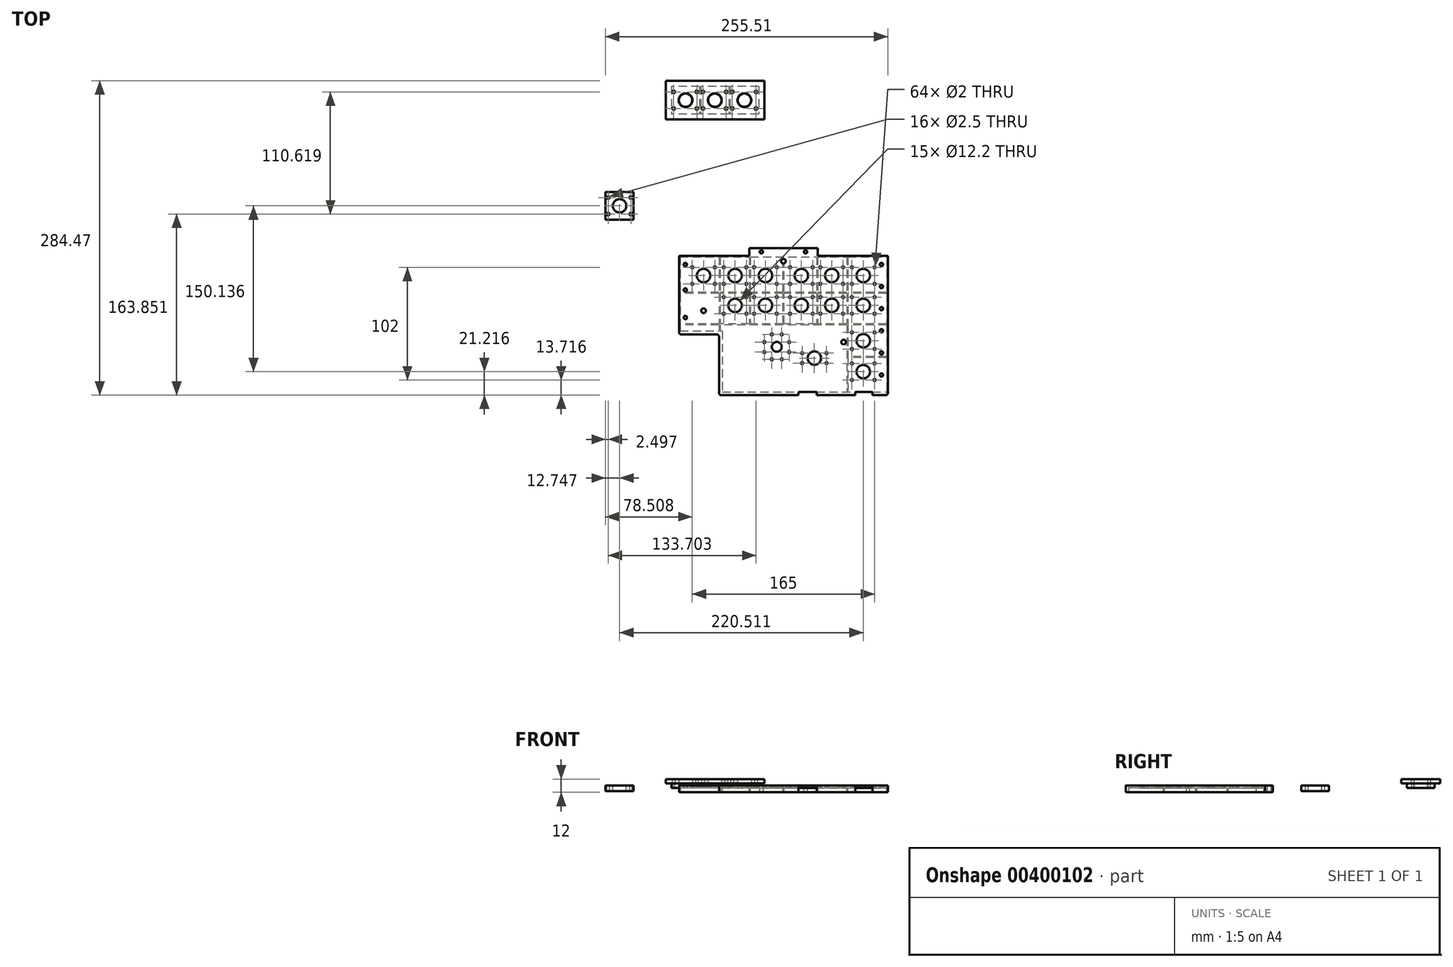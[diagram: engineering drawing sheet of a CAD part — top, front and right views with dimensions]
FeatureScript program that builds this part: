
annotation { "Feature Type Name" : "Feature", "Feature Type Description" : "" }
export const myFeature = defineFeature(function(context is Context, id is Id, definition is map)
    precondition{}
    {
        {
            var Q0;
            Q0=qCreatedBy(makeId("Top.planeOp"),FACE);
            var sketch = newSketch(context, id + "F0", { "sketchPlane" : qUnion([Q0])});
            skLineSegment(sketch, "E0.bottom", {"start": v(7.75, 12.5) * mm, "end": v(-7.75, 12.5) * mm});
            skLineSegment(sketch, "E0.top", {"start": v(7.75, -12.5) * mm, "end": v(-7.75, -12.5) * mm});
            skLineSegment(sketch, "E0.left", {"start": v(7.75, 12.5) * mm, "end": v(7.75, -12.5) * mm});
            skLineSegment(sketch, "E0.right", {"start": v(-7.75, 12.5) * mm, "end": v(-7.75, -12.5) * mm});
            skPoint(sketch, "E0.middle", {"position": v(0, 0) * mm});
            skLineSegment(sketch, "E1.bottom", {"start": v(-7.75, 12.5) * mm, "end": v(-12.75, 12.5) * mm});
            skLineSegment(sketch, "E1.top", {"start": v(-7.75, -12.5) * mm, "end": v(-12.75, -12.5) * mm});
            skLineSegment(sketch, "E1.right", {"start": v(-12.75, 12.5) * mm, "end": v(-12.75, -12.5) * mm});
            skLineSegment(sketch, "E2.bottom", {"start": v(7.75, 12.5) * mm, "end": v(12.75, 12.5) * mm});
            skLineSegment(sketch, "E2.top", {"start": v(7.75, -12.5) * mm, "end": v(12.75, -12.5) * mm});
            skLineSegment(sketch, "E2.right", {"start": v(12.75, 12.5) * mm, "end": v(12.75, -12.5) * mm});
            skCircle(sketch, "E3", {"center": v(-10.75, 7.5) * mm, "radius": 0.9 * mm});
            skPoint(sketch, "E3.centerSnap0", {"position": v(-10.25, 12.5) * mm});
            skCircle(sketch, "E4", {"center": v(-10.75, -7.5) * mm, "radius": 0.9 * mm});
            skCircle(sketch, "E5", {"center": v(10.25, 7.5) * mm, "radius": 0.9 * mm});
            skPoint(sketch, "E5.centerSnap0", {"position": v(10.25, 12.5) * mm});
            skCircle(sketch, "E6", {"center": v(10.25, -7.5) * mm, "radius": 0.9 * mm});
            skCircle(sketch, "E7", {"center": v(0, 0) * mm, "radius": 6 * mm});
            skLineSegment(sketch, "E8.bottom", {"start": v(34.25, 12.5) * mm, "end": v(18.75, 12.5) * mm});
            skLineSegment(sketch, "E8.top", {"start": v(34.25, -12.5) * mm, "end": v(18.75, -12.5) * mm});
            skLineSegment(sketch, "E8.left", {"start": v(34.25, 12.5) * mm, "end": v(34.25, -12.5) * mm});
            skLineSegment(sketch, "E8.right", {"start": v(18.75, 12.5) * mm, "end": v(18.75, -12.5) * mm});
            skPoint(sketch, "E8.middle", {"position": v(26.5, 0) * mm});
            skLineSegment(sketch, "E9.bottom", {"start": v(18.75, 12.5) * mm, "end": v(13.75, 12.5) * mm});
            skLineSegment(sketch, "E9.top", {"start": v(18.75, -12.5) * mm, "end": v(13.75, -12.5) * mm});
            skLineSegment(sketch, "E9.right", {"start": v(13.75, 12.5) * mm, "end": v(13.75, -12.5) * mm});
            skLineSegment(sketch, "E10.bottom", {"start": v(34.25, 12.5) * mm, "end": v(39.25, 12.5) * mm});
            skLineSegment(sketch, "E10.top", {"start": v(34.25, -12.5) * mm, "end": v(39.25, -12.5) * mm});
            skLineSegment(sketch, "E10.right", {"start": v(39.25, 12.5) * mm, "end": v(39.25, -12.5) * mm});
            skCircle(sketch, "E11", {"center": v(15.75, 7.5) * mm, "radius": 0.9 * mm});
            skPoint(sketch, "E11.centerSnap0", {"position": v(16.25, 12.5) * mm});
            skCircle(sketch, "E12", {"center": v(15.75, -7.5) * mm, "radius": 0.9 * mm});
            skCircle(sketch, "E13", {"center": v(36.75, 7.5) * mm, "radius": 0.9 * mm});
            skPoint(sketch, "E13.centerSnap0", {"position": v(36.75, 12.5) * mm});
            skCircle(sketch, "E14", {"center": v(36.75, -7.5) * mm, "radius": 0.9 * mm});
            skCircle(sketch, "E15", {"center": v(26.5, 0) * mm, "radius": 6 * mm});
            skLineSegment(sketch, "E16.bottom", {"start": v(61.25, 12.5) * mm, "end": v(45.25, 12.5) * mm});
            skLineSegment(sketch, "E16.top", {"start": v(61.25, -12.5) * mm, "end": v(45.25, -12.5) * mm});
            skLineSegment(sketch, "E16.left", {"start": v(61.25, 12.5) * mm, "end": v(61.25, -12.5) * mm});
            skLineSegment(sketch, "E16.right", {"start": v(45.25, 12.5) * mm, "end": v(45.25, -12.5) * mm});
            skPoint(sketch, "E16.middle", {"position": v(53.25, 0) * mm});
            skLineSegment(sketch, "E17.bottom", {"start": v(45.25, 12.5) * mm, "end": v(40.25, 12.5) * mm});
            skLineSegment(sketch, "E17.top", {"start": v(45.25, -12.5) * mm, "end": v(40.25, -12.5) * mm});
            skLineSegment(sketch, "E17.right", {"start": v(40.25, 12.5) * mm, "end": v(40.25, -12.5) * mm});
            skLineSegment(sketch, "E18.bottom", {"start": v(61.25, 12.5) * mm, "end": v(66.25, 12.5) * mm});
            skLineSegment(sketch, "E18.top", {"start": v(61.25, -12.5) * mm, "end": v(66.25, -12.5) * mm});
            skLineSegment(sketch, "E18.right", {"start": v(66.25, 12.5) * mm, "end": v(66.25, -12.5) * mm});
            skCircle(sketch, "E19", {"center": v(42.25, 7.5) * mm, "radius": 0.9 * mm});
            skPoint(sketch, "E19.centerSnap0", {"position": v(42.75, 12.5) * mm});
            skCircle(sketch, "E20", {"center": v(42.25, -7.5) * mm, "radius": 0.9 * mm});
            skCircle(sketch, "E21", {"center": v(63.75, 7.5) * mm, "radius": 0.9 * mm});
            skPoint(sketch, "E21.centerSnap0", {"position": v(63.75, 12.5) * mm});
            skCircle(sketch, "E22", {"center": v(63.75, -7.5) * mm, "radius": 0.9 * mm});
            skCircle(sketch, "E23", {"center": v(53.25, 0) * mm, "radius": 6 * mm});
            skSolve(sketch);
        }
        {
            var Q0;
            Q0=makeQuery(id+"F0.imprint","IMPRINT",FACE,{"disambiguationData":[TD([[makeQuery(id+"F0.imprint","IMPRINT",EDGE,{"derivedFrom":sQuery(id+"F0.wireOp",EDGE,"E0.bottom")}),1.0]])]});
            var Q1;
            Q1=makeQuery(id+"F0.imprint","IMPRINT",FACE,{"disambiguationData":[TD([[makeQuery(id+"F0.imprint","IMPRINT",EDGE,{"derivedFrom":sQuery(id+"F0.wireOp",EDGE,"E1.bottom")}),1.0]])]});
            var Q2;
            Q2=makeQuery(id+"F0.imprint","IMPRINT",FACE,{"disambiguationData":[TD([[makeQuery(id+"F0.imprint","IMPRINT",EDGE,{"derivedFrom":sQuery(id+"F0.wireOp",EDGE,"E2.bottom")}),-1.0]])]});
            var Q3;
            Q3=makeQuery(id+"F0.imprint","IMPRINT",FACE,{"disambiguationData":[TD([[makeQuery(id+"F0.imprint","IMPRINT",EDGE,{"derivedFrom":sQuery(id+"F0.wireOp",EDGE,"E9.bottom")}),1.0]])]});
            var Q4;
            Q4=makeQuery(id+"F0.imprint","IMPRINT",FACE,{"disambiguationData":[TD([[makeQuery(id+"F0.imprint","IMPRINT",EDGE,{"derivedFrom":sQuery(id+"F0.wireOp",EDGE,"E8.bottom")}),1.0]])]});
            var Q5;
            Q5=makeQuery(id+"F0.imprint","IMPRINT",FACE,{"disambiguationData":[TD([[makeQuery(id+"F0.imprint","IMPRINT",EDGE,{"derivedFrom":sQuery(id+"F0.wireOp",EDGE,"E10.bottom")}),-1.0]])]});
            var Q6;
            Q6=makeQuery(id+"F0.imprint","IMPRINT",FACE,{"disambiguationData":[TD([[makeQuery(id+"F0.imprint","IMPRINT",EDGE,{"derivedFrom":sQuery(id+"F0.wireOp",EDGE,"E17.bottom")}),1.0]])]});
            var Q7;
            Q7=makeQuery(id+"F0.imprint","IMPRINT",FACE,{"disambiguationData":[TD([[makeQuery(id+"F0.imprint","IMPRINT",EDGE,{"derivedFrom":sQuery(id+"F0.wireOp",EDGE,"E16.bottom")}),1.0]])]});
            var Q8;
            Q8=makeQuery(id+"F0.imprint","IMPRINT",FACE,{"disambiguationData":[TD([[makeQuery(id+"F0.imprint","IMPRINT",EDGE,{"derivedFrom":sQuery(id+"F0.wireOp",EDGE,"E18.bottom")}),-1.0]])]});
            extrude(context, id + "F1", {"entities" : qUnion([Q0, Q1, Q2, Q3, Q4, Q5, Q6, Q7, Q8]), "depth" : 4 * mm});
        }
        {
            var Q0;
            Q0=makeQuery(id+"F1.opExtrude","CAP_FACE",FACE,{"disambiguationData":[OSD([sQuery(id+"F0.wireOp",EDGE,"E0.bottom"),sQuery(id+"F0.wireOp",EDGE,"E0.top"),sQuery(id+"F0.wireOp",EDGE,"E1.bottom"),sQuery(id+"F0.wireOp",EDGE,"E1.top"),sQuery(id+"F0.wireOp",EDGE,"E1.right"),sQuery(id+"F0.wireOp",EDGE,"E2.bottom"),sQuery(id+"F0.wireOp",EDGE,"E2.top"),sQuery(id+"F0.wireOp",EDGE,"E2.right"),sQuery(id+"F0.wireOp",EDGE,"E3"),sQuery(id+"F0.wireOp",EDGE,"E4"),sQuery(id+"F0.wireOp",EDGE,"E5"),sQuery(id+"F0.wireOp",EDGE,"E6"),sQuery(id+"F0.wireOp",EDGE,"E7")])],"isStart":false});
            var sketch = newSketch(context, id + "F2", { "sketchPlane" : qUnion([Q0])});
            skLineSegment(sketch, "E24.bottom", {"start": v(-17.75, 17.5) * mm, "end": v(71.25, 17.5) * mm});
            skLineSegment(sketch, "E24.top", {"start": v(-17.75, -17.5) * mm, "end": v(71.25, -17.5) * mm});
            skLineSegment(sketch, "E24.left", {"start": v(-17.75, 17.5) * mm, "end": v(-17.75, -17.5) * mm});
            skLineSegment(sketch, "E24.right", {"start": v(71.25, 17.5) * mm, "end": v(71.25, -17.5) * mm});
            skCircle(sketch, "E25", {"center": v(-10.75, 7.5) * mm, "radius": 1.25 * mm});
            skCircle(sketch, "E26", {"center": v(-10.75, -7.5) * mm, "radius": 1.25 * mm});
            skCircle(sketch, "E27", {"center": v(10.25, -7.5) * mm, "radius": 1.25 * mm});
            skCircle(sketch, "E28", {"center": v(10.25, 7.5) * mm, "radius": 1.25 * mm});
            skCircle(sketch, "E29", {"center": v(15.75, 7.5) * mm, "radius": 1.25 * mm});
            skCircle(sketch, "E30", {"center": v(15.75, -7.5) * mm, "radius": 1.25 * mm});
            skCircle(sketch, "E31", {"center": v(36.75, -7.5) * mm, "radius": 1.25 * mm});
            skCircle(sketch, "E32", {"center": v(0, 0) * mm, "radius": 6.25 * mm});
            skCircle(sketch, "E33", {"center": v(26.5, 0) * mm, "radius": 6.25 * mm});
            skCircle(sketch, "E34", {"center": v(53.25, 0) * mm, "radius": 6.25 * mm});
            skCircle(sketch, "E35", {"center": v(36.75, 7.5) * mm, "radius": 1.25 * mm});
            skCircle(sketch, "E36", {"center": v(42.25, 7.5) * mm, "radius": 1.25 * mm});
            skCircle(sketch, "E37", {"center": v(42.25, -7.5) * mm, "radius": 1.25 * mm});
            skCircle(sketch, "E38", {"center": v(63.75, 7.5) * mm, "radius": 1.25 * mm});
            skCircle(sketch, "E39", {"center": v(63.75, -7.5) * mm, "radius": 1.25 * mm});
            skSolve(sketch);
        }
        {
            var Q0;
            Q0=qSketchRegion(id+"F2",true);
            extrude(context, id + "F3", {"entities" : qUnion([Q0]), "depth" : 4 * mm});
        }
        {
            var Q0;
            Q0=qCreatedBy(makeId("Top.planeOp"),FACE);
            var sketch = newSketch(context, id + "F4", { "sketchPlane" : qUnion([Q0])});
            skLineSegment(sketch, "E40.bottom", {"start": v(3.56, -143.75) * mm, "end": v(29.06, -143.75) * mm, "construction": true});
            skLineSegment(sketch, "E40.top", {"start": v(3.56, -173.75) * mm, "end": v(29.06, -173.75) * mm, "construction": true});
            skLineSegment(sketch, "E40.left", {"start": v(3.56, -143.75) * mm, "end": v(3.56, -173.75) * mm, "construction": true});
            skLineSegment(sketch, "E40.right", {"start": v(29.06, -143.75) * mm, "end": v(29.06, -173.75) * mm, "construction": true});
            skLineSegment(sketch, "E41.bottom", {"start": v(32.06, -143.75) * mm, "end": v(57.56, -143.75) * mm, "construction": true});
            skLineSegment(sketch, "E41.top", {"start": v(32.06, -173.75) * mm, "end": v(57.56, -173.75) * mm, "construction": true});
            skLineSegment(sketch, "E41.left", {"start": v(32.06, -143.75) * mm, "end": v(32.06, -173.75) * mm, "construction": true});
            skLineSegment(sketch, "E41.right", {"start": v(57.56, -143.75) * mm, "end": v(57.56, -173.75) * mm, "construction": true});
            skLineSegment(sketch, "E42.bottom", {"start": v(119.56, -143.75) * mm, "end": v(145.06, -143.75) * mm, "construction": true});
            skLineSegment(sketch, "E42.top", {"start": v(119.56, -173.75) * mm, "end": v(145.06, -173.75) * mm, "construction": true});
            skLineSegment(sketch, "E42.left", {"start": v(119.56, -143.75) * mm, "end": v(119.56, -173.75) * mm, "construction": true});
            skLineSegment(sketch, "E42.right", {"start": v(145.06, -143.75) * mm, "end": v(145.06, -173.75) * mm, "construction": true});
            skLineSegment(sketch, "E43.bottom", {"start": v(148.06, -143.75) * mm, "end": v(173.56, -143.75) * mm, "construction": true});
            skLineSegment(sketch, "E43.top", {"start": v(148.06, -173.75) * mm, "end": v(173.56, -173.75) * mm, "construction": true});
            skLineSegment(sketch, "E43.left", {"start": v(148.06, -143.75) * mm, "end": v(148.06, -173.75) * mm, "construction": true});
            skLineSegment(sketch, "E43.right", {"start": v(173.56, -143.75) * mm, "end": v(173.56, -173.75) * mm, "construction": true});
            skLineSegment(sketch, "E44.top", {"start": v(148.06, -206.75) * mm, "end": v(173.56, -206.75) * mm, "construction": true});
            skLineSegment(sketch, "E45.bottom", {"start": v(148.06, -209.25) * mm, "end": v(173.56, -209.25) * mm, "construction": true});
            skLineSegment(sketch, "E45.top", {"start": v(148.06, -239.25) * mm, "end": v(173.56, -239.25) * mm, "construction": true});
            skLineSegment(sketch, "E45.left", {"start": v(148.06, -209.25) * mm, "end": v(148.06, -239.25) * mm, "construction": true});
            skLineSegment(sketch, "E45.right", {"start": v(173.56, -209.25) * mm, "end": v(173.56, -239.25) * mm, "construction": true});
            skLineSegment(sketch, "E46.bottom", {"start": v(-4.94, -140.75) * mm, "end": v(182.06, -140.75) * mm});
            skLineSegment(sketch, "E46.top", {"start": v(33.28, -263.97) * mm, "end": v(182.06, -263.97) * mm});
            skLineSegment(sketch, "E46.left", {"start": v(-4.94, -140.75) * mm, "end": v(-4.94, -208.97) * mm});
            skLineSegment(sketch, "E46.right", {"start": v(182.06, -140.75) * mm, "end": v(182.06, -263.97) * mm});
            skLineSegment(sketch, "E47", {"start": v(-4.94, -208.97) * mm, "end": v(33.28, -208.97) * mm});
            skLineSegment(sketch, "E48", {"start": v(33.28, -208.97) * mm, "end": v(33.28, -263.97) * mm});
            skLineSegment(sketch, "E49.bottom", {"start": v(-67.45, -83.12) * mm, "end": v(-51.95, -83.12) * mm});
            skLineSegment(sketch, "E49.top", {"start": v(-67.45, -108.12) * mm, "end": v(-51.95, -108.12) * mm});
            skLineSegment(sketch, "E49.left", {"start": v(-67.45, -83.12) * mm, "end": v(-67.45, -108.12) * mm});
            skLineSegment(sketch, "E49.right", {"start": v(-51.95, -83.12) * mm, "end": v(-51.95, -108.12) * mm});
            skLineSegment(sketch, "E50.bottom", {"start": v(-51.95, -83.12) * mm, "end": v(-46.95, -83.12) * mm});
            skLineSegment(sketch, "E50.top", {"start": v(-51.95, -108.12) * mm, "end": v(-46.95, -108.12) * mm});
            skLineSegment(sketch, "E50.right", {"start": v(-46.95, -83.12) * mm, "end": v(-46.95, -108.12) * mm});
            skLineSegment(sketch, "E51.bottom", {"start": v(-67.45, -83.12) * mm, "end": v(-72.45, -83.12) * mm});
            skLineSegment(sketch, "E51.top", {"start": v(-67.45, -108.12) * mm, "end": v(-72.45, -108.12) * mm});
            skLineSegment(sketch, "E51.right", {"start": v(-72.45, -83.12) * mm, "end": v(-72.45, -108.12) * mm});
            skCircle(sketch, "E52", {"center": v(-59.7, -95.62) * mm, "radius": 6.1 * mm});
            skPoint(sketch, "E52.centerSnap0", {"position": v(-67.45, -95.62) * mm});
            skPoint(sketch, "E52.centerSnap1", {"position": v(-59.7, -83.12) * mm});
            skCircle(sketch, "E53", {"center": v(-69.95, -88.12) * mm, "radius": 1.25 * mm});
            skPoint(sketch, "E53.centerSnap0", {"position": v(-69.95, -83.12) * mm});
            skCircle(sketch, "E54", {"center": v(-69.95, -103.12) * mm, "radius": 1.25 * mm});
            skCircle(sketch, "E55", {"center": v(-49.45, -88.12) * mm, "radius": 1.25 * mm});
            skPoint(sketch, "E55.centerSnap0", {"position": v(-49.45, -83.12) * mm});
            skCircle(sketch, "E56", {"center": v(-49.45, -103.12) * mm, "radius": 1.25 * mm});
            skLineSegment(sketch, "E57.bottom", {"start": v(3.56, -146.25) * mm, "end": v(8.56, -146.25) * mm, "construction": true});
            skLineSegment(sketch, "E57.top", {"start": v(3.56, -171.25) * mm, "end": v(8.56, -171.25) * mm, "construction": true});
            skLineSegment(sketch, "E57.left", {"start": v(3.56, -146.25) * mm, "end": v(3.56, -171.25) * mm, "construction": true});
            skLineSegment(sketch, "E57.right", {"start": v(8.56, -146.25) * mm, "end": v(8.56, -171.25) * mm, "construction": true});
            skLineSegment(sketch, "E58.bottom", {"start": v(29.06, -146.25) * mm, "end": v(24.06, -146.25) * mm, "construction": true});
            skLineSegment(sketch, "E58.top", {"start": v(29.06, -171.25) * mm, "end": v(24.06, -171.25) * mm, "construction": true});
            skLineSegment(sketch, "E58.left", {"start": v(29.06, -146.25) * mm, "end": v(29.06, -171.25) * mm, "construction": true});
            skLineSegment(sketch, "E58.right", {"start": v(24.06, -146.25) * mm, "end": v(24.06, -171.25) * mm, "construction": true});
            skCircle(sketch, "E59", {"center": v(6.06, -151.25) * mm, "radius": 1 * mm});
            skPoint(sketch, "E59.centerSnap0", {"position": v(6.06, -146.25) * mm});
            skCircle(sketch, "E60", {"center": v(6.06, -166.25) * mm, "radius": 1 * mm});
            skCircle(sketch, "E61", {"center": v(16.3, -158.75) * mm, "radius": 6.1 * mm});
            skPoint(sketch, "E61.centerSnap0", {"position": v(8.56, -158.75) * mm});
            skPoint(sketch, "E61.centerSnap1", {"position": v(16.3, -143.75) * mm});
            skCircle(sketch, "E62", {"center": v(26.56, -151.25) * mm, "radius": 1 * mm});
            skPoint(sketch, "E62.centerSnap0", {"position": v(26.56, -146.25) * mm});
            skCircle(sketch, "E63", {"center": v(26.56, -166.25) * mm, "radius": 1 * mm});
            skCircle(sketch, "E64", {"center": v(105.56, -228.97) * mm, "radius": 1 * mm});
            skCircle(sketch, "E65", {"center": v(105.56, -237.97) * mm, "radius": 1 * mm});
            skCircle(sketch, "E66", {"center": v(127.56, -228.97) * mm, "radius": 1 * mm});
            skCircle(sketch, "E67", {"center": v(127.56, -237.97) * mm, "radius": 1 * mm});
            skLineSegment(sketch, "E68.bottom", {"start": v(151.56, -240.25) * mm, "end": v(173.56, -240.25) * mm, "construction": true});
            skLineSegment(sketch, "E68.top", {"start": v(151.56, -262.25) * mm, "end": v(173.56, -262.25) * mm, "construction": true});
            skLineSegment(sketch, "E68.left", {"start": v(151.56, -240.25) * mm, "end": v(151.56, -262.25) * mm, "construction": true});
            skLineSegment(sketch, "E68.right", {"start": v(173.56, -240.25) * mm, "end": v(173.56, -262.25) * mm, "construction": true});
            skLineSegment(sketch, "E69.bottom", {"start": v(154.8, -239.75) * mm, "end": v(166.8, -239.75) * mm, "construction": true});
            skLineSegment(sketch, "E69.top", {"start": v(154.8, -251.75) * mm, "end": v(166.8, -251.75) * mm, "construction": true});
            skLineSegment(sketch, "E69.left", {"start": v(154.8, -239.75) * mm, "end": v(154.8, -251.75) * mm, "construction": true});
            skLineSegment(sketch, "E69.right", {"start": v(166.8, -239.75) * mm, "end": v(166.8, -251.75) * mm, "construction": true});
            skLineSegment(sketch, "E70.bottom", {"start": v(32.06, -146.25) * mm, "end": v(37.06, -146.25) * mm, "construction": true});
            skLineSegment(sketch, "E70.top", {"start": v(32.06, -171.25) * mm, "end": v(37.06, -171.25) * mm, "construction": true});
            skLineSegment(sketch, "E70.left", {"start": v(32.06, -146.25) * mm, "end": v(32.06, -171.25) * mm, "construction": true});
            skLineSegment(sketch, "E70.right", {"start": v(37.06, -146.25) * mm, "end": v(37.06, -171.25) * mm, "construction": true});
            skLineSegment(sketch, "E71.bottom", {"start": v(57.56, -146.25) * mm, "end": v(52.56, -146.25) * mm, "construction": true});
            skLineSegment(sketch, "E71.top", {"start": v(57.56, -171.25) * mm, "end": v(52.56, -171.25) * mm, "construction": true});
            skLineSegment(sketch, "E71.left", {"start": v(57.56, -146.25) * mm, "end": v(57.56, -171.25) * mm, "construction": true});
            skLineSegment(sketch, "E71.right", {"start": v(52.56, -146.25) * mm, "end": v(52.56, -171.25) * mm, "construction": true});
            skCircle(sketch, "E72", {"center": v(34.56, -151.25) * mm, "radius": 1 * mm});
            skPoint(sketch, "E72.centerSnap0", {"position": v(34.56, -146.25) * mm});
            skCircle(sketch, "E73", {"center": v(34.56, -166.25) * mm, "radius": 1 * mm});
            skCircle(sketch, "E74", {"center": v(55.06, -151.25) * mm, "radius": 1 * mm});
            skPoint(sketch, "E74.centerSnap0", {"position": v(55.06, -146.25) * mm});
            skCircle(sketch, "E75", {"center": v(55.06, -166.25) * mm, "radius": 1 * mm});
            skCircle(sketch, "E76", {"center": v(44.8, -158.75) * mm, "radius": 6.1 * mm});
            skPoint(sketch, "E76.centerSnap0", {"position": v(37.06, -158.75) * mm});
            skPoint(sketch, "E76.centerSnap1", {"position": v(44.8, -143.75) * mm});
            skLineSegment(sketch, "E77.bottom", {"start": v(119.56, -146.25) * mm, "end": v(124.56, -146.25) * mm, "construction": true});
            skLineSegment(sketch, "E77.top", {"start": v(119.56, -171.25) * mm, "end": v(124.56, -171.25) * mm, "construction": true});
            skLineSegment(sketch, "E77.left", {"start": v(119.56, -146.25) * mm, "end": v(119.56, -171.25) * mm, "construction": true});
            skLineSegment(sketch, "E77.right", {"start": v(124.56, -146.25) * mm, "end": v(124.56, -171.25) * mm, "construction": true});
            skLineSegment(sketch, "E78.bottom", {"start": v(145.06, -146.25) * mm, "end": v(140.06, -146.25) * mm, "construction": true});
            skLineSegment(sketch, "E78.top", {"start": v(145.06, -171.25) * mm, "end": v(140.06, -171.25) * mm, "construction": true});
            skLineSegment(sketch, "E78.left", {"start": v(145.06, -146.25) * mm, "end": v(145.06, -171.25) * mm, "construction": true});
            skLineSegment(sketch, "E78.right", {"start": v(140.06, -146.25) * mm, "end": v(140.06, -171.25) * mm, "construction": true});
            skLineSegment(sketch, "E79.bottom", {"start": v(148.06, -146.25) * mm, "end": v(153.06, -146.25) * mm, "construction": true});
            skLineSegment(sketch, "E79.top", {"start": v(148.06, -171.25) * mm, "end": v(153.06, -171.25) * mm, "construction": true});
            skLineSegment(sketch, "E79.left", {"start": v(148.06, -146.25) * mm, "end": v(148.06, -171.25) * mm, "construction": true});
            skLineSegment(sketch, "E79.right", {"start": v(153.06, -146.25) * mm, "end": v(153.06, -171.25) * mm, "construction": true});
            skLineSegment(sketch, "E80.bottom", {"start": v(173.56, -146.25) * mm, "end": v(168.56, -146.25) * mm, "construction": true});
            skLineSegment(sketch, "E80.top", {"start": v(173.56, -171.25) * mm, "end": v(168.56, -171.25) * mm, "construction": true});
            skLineSegment(sketch, "E80.left", {"start": v(173.56, -146.25) * mm, "end": v(173.56, -171.25) * mm, "construction": true});
            skLineSegment(sketch, "E80.right", {"start": v(168.56, -146.25) * mm, "end": v(168.56, -171.25) * mm, "construction": true});
            skLineSegment(sketch, "E81.top", {"start": v(148.06, -204.25) * mm, "end": v(153.06, -204.25) * mm, "construction": true});
            skLineSegment(sketch, "E82.top", {"start": v(173.56, -204.25) * mm, "end": v(168.56, -204.25) * mm, "construction": true});
            skLineSegment(sketch, "E83.bottom", {"start": v(148.06, -205.25) * mm, "end": v(153.06, -205.25) * mm, "construction": true});
            skLineSegment(sketch, "E83.top", {"start": v(148.06, -230.25) * mm, "end": v(153.06, -230.25) * mm, "construction": true});
            skLineSegment(sketch, "E83.left", {"start": v(148.06, -205.25) * mm, "end": v(148.06, -230.25) * mm, "construction": true});
            skLineSegment(sketch, "E83.right", {"start": v(153.06, -205.25) * mm, "end": v(153.06, -230.25) * mm, "construction": true});
            skLineSegment(sketch, "E84.bottom", {"start": v(173.56, -205.25) * mm, "end": v(168.56, -205.25) * mm, "construction": true});
            skLineSegment(sketch, "E84.top", {"start": v(173.56, -230.25) * mm, "end": v(168.56, -230.25) * mm, "construction": true});
            skLineSegment(sketch, "E84.left", {"start": v(173.56, -205.25) * mm, "end": v(173.56, -230.25) * mm, "construction": true});
            skLineSegment(sketch, "E84.right", {"start": v(168.56, -205.25) * mm, "end": v(168.56, -230.25) * mm, "construction": true});
            skCircle(sketch, "E85", {"center": v(62.06, -178.25) * mm, "radius": 1 * mm});
            skCircle(sketch, "E86", {"center": v(62.06, -193.25) * mm, "radius": 1 * mm});
            skCircle(sketch, "E87", {"center": v(82.56, -178.25) * mm, "radius": 1 * mm});
            skCircle(sketch, "E88", {"center": v(82.56, -193.25) * mm, "radius": 1 * mm});
            skCircle(sketch, "E89", {"center": v(72.3, -185.75) * mm, "radius": 6.1 * mm});
            skCircle(sketch, "E90", {"center": v(82.56, -223.25) * mm, "radius": 4.5 * mm});
            skCircle(sketch, "E91", {"center": v(71.3, -219) * mm, "radius": 1 * mm});
            skCircle(sketch, "E92", {"center": v(71.3, -228) * mm, "radius": 1 * mm});
            skCircle(sketch, "E93", {"center": v(93.8, -219) * mm, "radius": 1 * mm});
            skCircle(sketch, "E94", {"center": v(93.8, -228) * mm, "radius": 1 * mm});
            skCircle(sketch, "E95", {"center": v(94.56, -178.25) * mm, "radius": 1 * mm});
            skCircle(sketch, "E96", {"center": v(94.56, -193.25) * mm, "radius": 1 * mm});
            skCircle(sketch, "E97", {"center": v(115.06, -178.25) * mm, "radius": 1 * mm});
            skCircle(sketch, "E98", {"center": v(115.06, -193.25) * mm, "radius": 1 * mm});
            skCircle(sketch, "E99", {"center": v(122.06, -151.25) * mm, "radius": 1 * mm});
            skPoint(sketch, "E99.centerSnap0", {"position": v(122.06, -146.25) * mm});
            skCircle(sketch, "E100", {"center": v(122.06, -166.25) * mm, "radius": 1 * mm});
            skCircle(sketch, "E101", {"center": v(132.3, -158.75) * mm, "radius": 6.1 * mm});
            skPoint(sketch, "E101.centerSnap0", {"position": v(124.56, -158.75) * mm});
            skPoint(sketch, "E101.centerSnap1", {"position": v(132.3, -143.75) * mm});
            skCircle(sketch, "E102", {"center": v(142.56, -151.25) * mm, "radius": 1 * mm});
            skPoint(sketch, "E102.centerSnap0", {"position": v(142.56, -146.25) * mm});
            skCircle(sketch, "E103", {"center": v(142.56, -166.25) * mm, "radius": 1 * mm});
            skCircle(sketch, "E104", {"center": v(150.56, -151.25) * mm, "radius": 1 * mm});
            skPoint(sketch, "E104.centerSnap0", {"position": v(150.56, -146.25) * mm});
            skCircle(sketch, "E105", {"center": v(150.56, -166.25) * mm, "radius": 1 * mm});
            skCircle(sketch, "E106", {"center": v(171.06, -151.25) * mm, "radius": 1 * mm});
            skPoint(sketch, "E106.centerSnap0", {"position": v(171.06, -146.25) * mm});
            skCircle(sketch, "E107", {"center": v(171.06, -166.25) * mm, "radius": 1 * mm});
            skCircle(sketch, "E108", {"center": v(160.8, -158.75) * mm, "radius": 6.1 * mm});
            skPoint(sketch, "E108.centerSnap0", {"position": v(153.06, -158.75) * mm});
            skPoint(sketch, "E108.centerSnap1", {"position": v(160.8, -143.75) * mm});
            skCircle(sketch, "E109", {"center": v(16.3, -190.57) * mm, "radius": 2.1 * mm});
            skCircle(sketch, "E110", {"center": v(143.06, -218.97) * mm, "radius": 2.1 * mm});
            skCircle(sketch, "E111", {"center": v(150.56, -210.25) * mm, "radius": 1 * mm});
            skPoint(sketch, "E111.centerSnap0", {"position": v(150.56, -205.25) * mm});
            skCircle(sketch, "E112", {"center": v(150.56, -225.25) * mm, "radius": 1 * mm});
            skCircle(sketch, "E113", {"center": v(171.06, -210.25) * mm, "radius": 1 * mm});
            skPoint(sketch, "E113.centerSnap0", {"position": v(171.06, -205.25) * mm});
            skCircle(sketch, "E114", {"center": v(171.06, -225.25) * mm, "radius": 1 * mm});
            skCircle(sketch, "E115", {"center": v(160.8, -217.75) * mm, "radius": 6.1 * mm});
            skPoint(sketch, "E115.centerSnap0", {"position": v(153.06, -217.75) * mm});
            skCircle(sketch, "E116", {"center": v(160.8, -245.75) * mm, "radius": 6.1 * mm});
            skPoint(sketch, "E116.centerSnap0", {"position": v(160.8, -239.75) * mm});
            skPoint(sketch, "E116.centerSnap1", {"position": v(154.8, -245.75) * mm});
            skCircle(sketch, "E117", {"center": v(-0.2, -148.75) * mm, "radius": 1.5 * mm});
            skCircle(sketch, "E118", {"center": v(-0.2, -171.75) * mm, "radius": 1.5 * mm});
            skCircle(sketch, "E119", {"center": v(177.3, -208.75) * mm, "radius": 1.5 * mm});
            skCircle(sketch, "E120", {"center": v(177.3, -228.75) * mm, "radius": 1.5 * mm});
            skCircle(sketch, "E121", {"center": v(177.3, -248.75) * mm, "radius": 1.5 * mm});
            skCircle(sketch, "E122", {"center": v(177.3, -168.75) * mm, "radius": 1.5 * mm});
            skCircle(sketch, "E123", {"center": v(177.3, -188.75) * mm, "radius": 1.5 * mm});
            skCircle(sketch, "E124", {"center": v(177.3, -148.75) * mm, "radius": 1.5 * mm});
            skCircle(sketch, "E125", {"center": v(150.56, -238.25) * mm, "radius": 1 * mm});
            skCircle(sketch, "E126", {"center": v(150.56, -253.25) * mm, "radius": 1 * mm});
            skCircle(sketch, "E127", {"center": v(171.06, -238.25) * mm, "radius": 1 * mm});
            skCircle(sketch, "E128", {"center": v(171.06, -253.25) * mm, "radius": 1 * mm});
            skCircle(sketch, "E129", {"center": v(-0.2, -196.75) * mm, "radius": 1.5 * mm});
            skLineSegment(sketch, "E130.bottom", {"start": v(58.56, -140.75) * mm, "end": v(118.56, -140.75) * mm});
            skLineSegment(sketch, "E130.top", {"start": v(58.56, -133.75) * mm, "end": v(118.56, -133.75) * mm});
            skLineSegment(sketch, "E130.left", {"start": v(58.56, -140.75) * mm, "end": v(58.56, -133.75) * mm});
            skLineSegment(sketch, "E130.right", {"start": v(118.56, -140.75) * mm, "end": v(118.56, -133.75) * mm});
            skCircle(sketch, "E131", {"center": v(68.56, -137.25) * mm, "radius": 1.5 * mm});
            skCircle(sketch, "E132", {"center": v(108.56, -137.25) * mm, "radius": 1.5 * mm});
            skCircle(sketch, "E133", {"center": v(116.56, -233.47) * mm, "radius": 6.1 * mm});
            skCircle(sketch, "E134", {"center": v(82.56, -223.25) * mm, "radius": 12.5 * mm, "construction": true});
            skCircle(sketch, "E135", {"center": v(44.8, -185.75) * mm, "radius": 6.1 * mm});
            skCircle(sketch, "E136", {"center": v(34.56, -178.25) * mm, "radius": 1 * mm});
            skCircle(sketch, "E137", {"center": v(34.56, -193.25) * mm, "radius": 1 * mm});
            skCircle(sketch, "E138", {"center": v(55.06, -178.25) * mm, "radius": 1 * mm});
            skCircle(sketch, "E139", {"center": v(55.06, -193.25) * mm, "radius": 1 * mm});
            skCircle(sketch, "E140", {"center": v(122.06, -193.25) * mm, "radius": 1 * mm});
            skCircle(sketch, "E141", {"center": v(142.56, -193.25) * mm, "radius": 1 * mm});
            skLineSegment(sketch, "E142", {"start": v(223.04, -262.25) * mm, "end": v(194.25, -262.25) * mm, "construction": true});
            skCircle(sketch, "E143", {"center": v(78.06, -212) * mm, "radius": 1 * mm});
            skCircle(sketch, "E144", {"center": v(87.06, -212) * mm, "radius": 1 * mm});
            skCircle(sketch, "E145", {"center": v(78.06, -234.5) * mm, "radius": 1 * mm});
            skCircle(sketch, "E146", {"center": v(87.06, -234.5) * mm, "radius": 1 * mm});
            skCircle(sketch, "E147", {"center": v(104.8, -185.75) * mm, "radius": 6.1 * mm});
            skCircle(sketch, "E148", {"center": v(132.3, -185.75) * mm, "radius": 6.1 * mm});
            skCircle(sketch, "E149", {"center": v(122.06, -178.25) * mm, "radius": 1 * mm});
            skCircle(sketch, "E150", {"center": v(142.56, -178.25) * mm, "radius": 1 * mm});
            skCircle(sketch, "E151", {"center": v(160.8, -185.75) * mm, "radius": 6.1 * mm});
            skCircle(sketch, "E152", {"center": v(150.56, -178.25) * mm, "radius": 1 * mm});
            skCircle(sketch, "E153", {"center": v(150.56, -193.25) * mm, "radius": 1 * mm});
            skCircle(sketch, "E154", {"center": v(171.06, -178.25) * mm, "radius": 1 * mm});
            skPoint(sketch, "E154.centerSnap0", {"position": v(171.06, -171.25) * mm});
            skCircle(sketch, "E155", {"center": v(171.06, -193.25) * mm, "radius": 1 * mm});
            skCircle(sketch, "E156", {"center": v(104.8, -158.75) * mm, "radius": 6.1 * mm});
            skCircle(sketch, "E157", {"center": v(115.06, -151.25) * mm, "radius": 1 * mm});
            skCircle(sketch, "E158", {"center": v(115.06, -166.25) * mm, "radius": 1 * mm});
            skCircle(sketch, "E159", {"center": v(94.56, -151.25) * mm, "radius": 1 * mm});
            skCircle(sketch, "E160", {"center": v(94.56, -166.25) * mm, "radius": 1 * mm});
            skCircle(sketch, "E161", {"center": v(72.3, -158.75) * mm, "radius": 6.1 * mm});
            skCircle(sketch, "E162", {"center": v(82.56, -151.25) * mm, "radius": 1 * mm});
            skCircle(sketch, "E163", {"center": v(82.56, -166.25) * mm, "radius": 1 * mm});
            skCircle(sketch, "E164", {"center": v(62.06, -151.25) * mm, "radius": 1 * mm});
            skCircle(sketch, "E165", {"center": v(62.06, -166.25) * mm, "radius": 1 * mm});
            skCircle(sketch, "E166", {"center": v(88.56, -145.75) * mm, "radius": 2.1 * mm});
            skSolve(sketch);
        }
        {
            var Q0;
            Q0=makeQuery(id+"F4.imprint","IMPRINT",FACE,{"disambiguationData":[TD([[makeQuery(id+"F4.imprint","IMPRINT",EDGE,{"derivedFrom":sQuery(id+"F4.wireOp",EDGE,"E49.bottom")}),-1.0]])]});
            var Q1;
            Q1=makeQuery(id+"F4.imprint","IMPRINT",FACE,{"disambiguationData":[TD([[makeQuery(id+"F4.imprint","IMPRINT",EDGE,{"derivedFrom":sQuery(id+"F4.wireOp",EDGE,"E51.bottom")}),1.0]])]});
            var Q2;
            Q2=makeQuery(id+"F4.imprint","IMPRINT",FACE,{"disambiguationData":[TD([[makeQuery(id+"F4.imprint","IMPRINT",EDGE,{"derivedFrom":sQuery(id+"F4.wireOp",EDGE,"E50.bottom")}),-1.0]])]});
            extrude(context, id + "F5", {"entities" : qUnion([Q0, Q1, Q2]), "oppositeDirection" : true, "depth" : 3 * mm});
        }
        {
            var Q0;
            Q0=qSketchRegion(id+"F4",true);
            extrude(context, id + "F6", {"entities" : qUnion([Q0]), "operationType" : NewBodyOperationType.ADD, "depth" : 2 * mm});
        }
        {
            var Q0;
            Q0=makeQuery(id+"F4.imprint","IMPRINT",FACE,{"disambiguationData":[TD([[makeQuery(id+"F4.imprint","IMPRINT",EDGE,{"derivedFrom":sQuery(id+"F4.wireOp",EDGE,"E46.bottom")}),-1.0]])]});
            var sketch = newSketch(context, id + "F7", { "sketchPlane" : qUnion([Q0])});
            skLineSegment(sketch, "E167", {"start": v(191, -174) * mm, "end": v(196.06, -174) * mm, "construction": true});
            skLineSegment(sketch, "E168", {"start": v(187.13, -202.5) * mm, "end": v(195.16, -202.5) * mm, "construction": true});
            skLineSegment(sketch, "E169", {"start": v(185.67, -231.87) * mm, "end": v(191.23, -231.87) * mm, "construction": true});
            skLineSegment(sketch, "E170", {"start": v(147.06, -137.55) * mm, "end": v(147.06, -134.13) * mm, "construction": true});
            skLineSegment(sketch, "E171", {"start": v(119.6, -132.5) * mm, "end": v(119.6, -129.45) * mm, "construction": true});
            skLineSegment(sketch, "E172", {"start": v(58.56, -132.83) * mm, "end": v(58.56, -129.85) * mm, "construction": true});
            skLineSegment(sketch, "E173", {"start": v(31.28, -136.19) * mm, "end": v(31.28, -132.5) * mm, "construction": true});
            skLineSegment(sketch, "E174.bottom", {"start": v(182.06, -174) * mm, "end": v(147.06, -174) * mm});
            skLineSegment(sketch, "E174.top", {"start": v(182.06, -175) * mm, "end": v(147.06, -175) * mm});
            skLineSegment(sketch, "E174.left", {"start": v(182.06, -174) * mm, "end": v(182.06, -175) * mm});
            skLineSegment(sketch, "E174.right", {"start": v(-4.94, -174) * mm, "end": v(-4.94, -175) * mm});
            skLineSegment(sketch, "E175.bottom", {"start": v(182.06, -202.5) * mm, "end": v(147.06, -202.5) * mm});
            skLineSegment(sketch, "E175.top", {"start": v(182.06, -203.5) * mm, "end": v(147.06, -203.5) * mm});
            skLineSegment(sketch, "E175.left", {"start": v(182.06, -202.5) * mm, "end": v(182.06, -203.5) * mm});
            skLineSegment(sketch, "E175.right", {"start": v(-4.94, -202.5) * mm, "end": v(-4.94, -203.5) * mm});
            skLineSegment(sketch, "E176", {"start": v(194.32, -140.75) * mm, "end": v(196.06, -263.96) * mm, "construction": true});
            skLineSegment(sketch, "E177", {"start": v(190.9, -263.96) * mm, "end": v(185.03, -263.96) * mm, "construction": true});
            skLineSegment(sketch, "E178.bottom", {"start": v(182.06, -231.87) * mm, "end": v(147.06, -231.87) * mm});
            skLineSegment(sketch, "E178.top", {"start": v(182.06, -232.87) * mm, "end": v(147.06, -232.87) * mm});
            skLineSegment(sketch, "E178.left", {"start": v(182.06, -231.87) * mm, "end": v(182.06, -232.87) * mm});
            skLineSegment(sketch, "E179", {"start": v(-4.94, -139.37) * mm, "end": v(-4.94, -137.02) * mm, "construction": true});
            skLineSegment(sketch, "E180", {"start": v(-7.3, -140.75) * mm, "end": v(-12.92, -140.75) * mm, "construction": true});
            skLineSegment(sketch, "E181.bottom", {"start": v(-4.94, -140.75) * mm, "end": v(146.06, -140.75) * mm});
            skLineSegment(sketch, "E181.top", {"start": v(-4.94, -141.75) * mm, "end": v(146.06, -141.75) * mm});
            skLineSegment(sketch, "E181.left", {"start": v(-4.94, -140.75) * mm, "end": v(-4.94, -141.75) * mm});
            skLineSegment(sketch, "E181.right", {"start": v(182.06, -140.75) * mm, "end": v(182.06, -141.75) * mm});
            skLineSegment(sketch, "E182.bottom", {"start": v(147.06, -140.75) * mm, "end": v(146.06, -140.75) * mm});
            skLineSegment(sketch, "E182.top", {"start": v(147.06, -263.96) * mm, "end": v(146.06, -263.96) * mm});
            skLineSegment(sketch, "E182.left", {"start": v(147.06, -141.75) * mm, "end": v(147.06, -174) * mm});
            skLineSegment(sketch, "E182.right", {"start": v(146.06, -141.75) * mm, "end": v(146.06, -174) * mm});
            skLineSegment(sketch, "E183.trimOffspring", {"start": v(147.06, -175) * mm, "end": v(147.06, -202.5) * mm});
            skLineSegment(sketch, "E184.trimOffspring", {"start": v(146.06, -174) * mm, "end": v(119.6, -174) * mm});
            skLineSegment(sketch, "E185.trimOffspring", {"start": v(146.06, -175) * mm, "end": v(146.06, -202.5) * mm});
            skLineSegment(sketch, "E186.trimOffspring", {"start": v(146.06, -175) * mm, "end": v(119.6, -175) * mm});
            skLineSegment(sketch, "E187.trimOffspring", {"start": v(146.06, -202.5) * mm, "end": v(119.6, -202.5) * mm});
            skLineSegment(sketch, "E188.trimOffspring", {"start": v(147.06, -203.5) * mm, "end": v(147.06, -231.87) * mm});
            skLineSegment(sketch, "E189.trimOffspring", {"start": v(146.06, -203.5) * mm, "end": v(58.56, -203.5) * mm});
            skLineSegment(sketch, "E190.trimOffspring", {"start": v(146.06, -203.5) * mm, "end": v(146.06, -263.96) * mm});
            skLineSegment(sketch, "E191.trimOffspring", {"start": v(147.06, -232.87) * mm, "end": v(147.06, -263.96) * mm});
            skLineSegment(sketch, "E192.trimOffspring", {"start": v(147.06, -140.75) * mm, "end": v(182.06, -140.75) * mm});
            skLineSegment(sketch, "E193.trimOffspring", {"start": v(147.06, -141.75) * mm, "end": v(182.06, -141.75) * mm});
            skLineSegment(sketch, "E194.bottom", {"start": v(119.6, -140.75) * mm, "end": v(118.6, -140.75) * mm});
            skLineSegment(sketch, "E194.left", {"start": v(119.6, -140.75) * mm, "end": v(119.6, -174) * mm});
            skLineSegment(sketch, "E194.right", {"start": v(118.6, -140.75) * mm, "end": v(118.6, -174) * mm});
            skLineSegment(sketch, "E195.top", {"start": v(89.06, -148.72) * mm, "end": v(88.06, -148.72) * mm});
            skLineSegment(sketch, "E195.left", {"start": v(89.06, -202.5) * mm, "end": v(89.06, -175) * mm});
            skLineSegment(sketch, "E195.right", {"start": v(88.06, -202.5) * mm, "end": v(88.06, -175) * mm});
            skLineSegment(sketch, "E196.bottom", {"start": v(58.56, -140.75) * mm, "end": v(57.56, -140.75) * mm});
            skLineSegment(sketch, "E196.left", {"start": v(58.56, -140.75) * mm, "end": v(58.56, -174) * mm});
            skLineSegment(sketch, "E196.right", {"start": v(57.56, -140.75) * mm, "end": v(57.56, -174) * mm});
            skLineSegment(sketch, "E197.trimOffspring", {"start": v(119.6, -175) * mm, "end": v(119.6, -202.5) * mm});
            skLineSegment(sketch, "E198.trimOffspring", {"start": v(118.6, -174) * mm, "end": v(89.06, -174) * mm});
            skLineSegment(sketch, "E199.trimOffspring", {"start": v(118.6, -175) * mm, "end": v(118.6, -202.5) * mm});
            skLineSegment(sketch, "E200.trimOffspring", {"start": v(118.6, -175) * mm, "end": v(89.06, -175) * mm});
            skLineSegment(sketch, "E201.trimOffspring", {"start": v(89.06, -174) * mm, "end": v(89.06, -148.72) * mm});
            skLineSegment(sketch, "E202.trimOffspring", {"start": v(88.06, -174) * mm, "end": v(58.56, -174) * mm});
            skLineSegment(sketch, "E203.trimOffspring", {"start": v(88.06, -174) * mm, "end": v(88.06, -148.72) * mm});
            skLineSegment(sketch, "E204.trimOffspring", {"start": v(88.06, -175) * mm, "end": v(58.56, -175) * mm});
            skLineSegment(sketch, "E205.trimOffspring", {"start": v(88.06, -202.5) * mm, "end": v(58.56, -202.5) * mm});
            skLineSegment(sketch, "E206.trimOffspring", {"start": v(118.6, -202.5) * mm, "end": v(89.06, -202.5) * mm});
            skLineSegment(sketch, "E207.bottom", {"start": v(31.28, -140.75) * mm, "end": v(30.28, -140.75) * mm});
            skLineSegment(sketch, "E207.left", {"start": v(31.28, -140.75) * mm, "end": v(31.28, -174) * mm});
            skLineSegment(sketch, "E207.right", {"start": v(30.28, -140.75) * mm, "end": v(30.28, -174) * mm});
            skLineSegment(sketch, "E208.trimOffspring", {"start": v(57.56, -202.5) * mm, "end": v(31.28, -202.5) * mm});
            skLineSegment(sketch, "E209.trimOffspring", {"start": v(58.56, -203.5) * mm, "end": v(31.28, -203.5) * mm});
            skLineSegment(sketch, "E210.trimOffspring", {"start": v(58.56, -175) * mm, "end": v(58.56, -202.5) * mm});
            skLineSegment(sketch, "E211.trimOffspring", {"start": v(57.56, -174) * mm, "end": v(31.28, -174) * mm});
            skLineSegment(sketch, "E212.trimOffspring", {"start": v(57.56, -175) * mm, "end": v(57.56, -202.5) * mm});
            skLineSegment(sketch, "E213.trimOffspring", {"start": v(57.56, -175) * mm, "end": v(31.28, -175) * mm});
            skLineSegment(sketch, "E214.trimOffspring", {"start": v(31.28, -175) * mm, "end": v(31.28, -202.5) * mm});
            skLineSegment(sketch, "E215.trimOffspring", {"start": v(30.28, -174) * mm, "end": v(-4.94, -174) * mm});
            skLineSegment(sketch, "E216.trimOffspring", {"start": v(30.28, -175) * mm, "end": v(30.28, -202.5) * mm});
            skLineSegment(sketch, "E217.trimOffspring", {"start": v(30.28, -175) * mm, "end": v(-4.94, -175) * mm});
            skLineSegment(sketch, "E218.trimOffspring", {"start": v(30.28, -202.5) * mm, "end": v(-4.94, -202.5) * mm});
            skLineSegment(sketch, "E219.top", {"start": v(31.28, -208.97) * mm, "end": v(30.28, -208.97) * mm});
            skLineSegment(sketch, "E219.left", {"start": v(31.28, -203.5) * mm, "end": v(31.28, -208.97) * mm});
            skLineSegment(sketch, "E219.right", {"start": v(30.28, -203.5) * mm, "end": v(30.28, -208.97) * mm});
            skLineSegment(sketch, "E220.trimOffspring", {"start": v(30.28, -203.5) * mm, "end": v(-4.94, -203.5) * mm});
            skLineSegment(sketch, "E221.bottom", {"start": v(99.56, -203.5) * mm, "end": v(98.56, -203.5) * mm});
            skSolve(sketch);
        }
        {
            var Q0;
            Q0=makeQuery(id+"F6.opExtrude","CAP_FACE",FACE,{"disambiguationData":[OSD([sQuery(id+"F4.wireOp",EDGE,"E46.bottom"),sQuery(id+"F4.wireOp",EDGE,"E46.top"),sQuery(id+"F4.wireOp",EDGE,"E46.left"),sQuery(id+"F4.wireOp",EDGE,"E46.right"),sQuery(id+"F4.wireOp",EDGE,"E47"),sQuery(id+"F4.wireOp",EDGE,"E48"),sQuery(id+"F4.wireOp",EDGE,"E59"),sQuery(id+"F4.wireOp",EDGE,"E60"),sQuery(id+"F4.wireOp",EDGE,"E61"),sQuery(id+"F4.wireOp",EDGE,"E62"),sQuery(id+"F4.wireOp",EDGE,"E63"),sQuery(id+"F4.wireOp",EDGE,"E64"),sQuery(id+"F4.wireOp",EDGE,"E65"),sQuery(id+"F4.wireOp",EDGE,"E66"),sQuery(id+"F4.wireOp",EDGE,"E67"),sQuery(id+"F4.wireOp",EDGE,"E72"),sQuery(id+"F4.wireOp",EDGE,"E73"),sQuery(id+"F4.wireOp",EDGE,"E74"),sQuery(id+"F4.wireOp",EDGE,"E75"),sQuery(id+"F4.wireOp",EDGE,"E76"),sQuery(id+"F4.wireOp",EDGE,"CMYmPeaI-4HkP-dSsT-ciCo-EBNArNxvabU4"),sQuery(id+"F4.wireOp",EDGE,"UfYHLVnG-ZsXc-hSsb-096B-xReGw4xjWMuN"),sQuery(id+"F4.wireOp",EDGE,"LR1Smqzz-4zCy-jBud-aIPe-T4FdCvFcucQ2"),sQuery(id+"F4.wireOp",EDGE,"ZbBtRst9-qfY5-xJJi-duYC-lclwT5zfDQth"),sQuery(id+"F4.wireOp",EDGE,"8mlmSCBx-nmsO-8ibw-fLZu-H13SXNY5Fta6"),sQuery(id+"F4.wireOp",EDGE,"E85"),sQuery(id+"F4.wireOp",EDGE,"E86"),sQuery(id+"F4.wireOp",EDGE,"E87"),sQuery(id+"F4.wireOp",EDGE,"E88"),sQuery(id+"F4.wireOp",EDGE,"E89"),sQuery(id+"F4.wireOp",EDGE,"E90"),sQuery(id+"F4.wireOp",EDGE,"E91"),sQuery(id+"F4.wireOp",EDGE,"E92"),sQuery(id+"F4.wireOp",EDGE,"E93"),sQuery(id+"F4.wireOp",EDGE,"E94"),sQuery(id+"F4.wireOp",EDGE,"VxGM9Us5-GGZY-iukY-QufE-Hgw7Eb7M8YLq"),sQuery(id+"F4.wireOp",EDGE,"SQwhu13T-8Qlf-M2A9-FjbU-sqE2fhrdCHsq"),sQuery(id+"F4.wireOp",EDGE,"boMX5wRL-iCUG-njbD-9Rz0-iznqWW2C3mA9"),sQuery(id+"F4.wireOp",EDGE,"8wUrnrco-ptQb-soB3-ZJPL-oLVazxcvUS0h"),sQuery(id+"F4.wireOp",EDGE,"HpmNjthl-ehj3-1CQD-7Ubw-BaRG0imoQFcp"),sQuery(id+"F4.wireOp",EDGE,"E95"),sQuery(id+"F4.wireOp",EDGE,"E96"),sQuery(id+"F4.wireOp",EDGE,"E97"),sQuery(id+"F4.wireOp",EDGE,"E98"),sQuery(id+"F4.wireOp",EDGE,"VaTJDDM9-VUwq-8Ub5-B3vK-8OZuGjwCmtKx"),sQuery(id+"F4.wireOp",EDGE,"E99"),sQuery(id+"F4.wireOp",EDGE,"E100"),sQuery(id+"F4.wireOp",EDGE,"E101"),sQuery(id+"F4.wireOp",EDGE,"E102"),sQuery(id+"F4.wireOp",EDGE,"E103"),sQuery(id+"F4.wireOp",EDGE,"E104"),sQuery(id+"F4.wireOp",EDGE,"E105"),sQuery(id+"F4.wireOp",EDGE,"E106"),sQuery(id+"F4.wireOp",EDGE,"E107"),sQuery(id+"F4.wireOp",EDGE,"E108"),sQuery(id+"F4.wireOp",EDGE,"FLjO8hJO-b9aV-ejTu-NQdn-92oojDJo2zOz"),sQuery(id+"F4.wireOp",EDGE,"a0hJ5jbA-nbqK-hj7D-t7WL-IcpDiukpPwzh"),sQuery(id+"F4.wireOp",EDGE,"Ryervvjx-vNoG-fDVS-CNAW-2For5iN3UFYN"),sQuery(id+"F4.wireOp",EDGE,"h7MID1Gx-mTQT-Sx65-6Eka-E6sNebulpS2X"),sQuery(id+"F4.wireOp",EDGE,"WRXfD2HC-k7r3-eJkd-8mHz-8ZkhsYc1BRgL"),sQuery(id+"F4.wireOp",EDGE,"E109"),sQuery(id+"F4.wireOp",EDGE,"E110"),sQuery(id+"F4.wireOp",EDGE,"E111"),sQuery(id+"F4.wireOp",EDGE,"E112"),sQuery(id+"F4.wireOp",EDGE,"E113"),sQuery(id+"F4.wireOp",EDGE,"E114"),sQuery(id+"F4.wireOp",EDGE,"E115"),sQuery(id+"F4.wireOp",EDGE,"i2m1gv8j-diLw-4k4K-fPdu-nWKSfx8HA4P4"),sQuery(id+"F4.wireOp",EDGE,"q3kUeOFW-MYc1-yF3y-feIh-HT3K9hYQvfPw"),sQuery(id+"F4.wireOp",EDGE,"E116"),sQuery(id+"F4.wireOp",EDGE,"0s6mQaFc-8NzZ-X89h-nX0r-AyVE9FRU5R3i"),sQuery(id+"F4.wireOp",EDGE,"E117"),sQuery(id+"F4.wireOp",EDGE,"OnnnS06f-s26S-AFDA-oTM6-wnMq7venfp2T"),sQuery(id+"F4.wireOp",EDGE,"V2efC4Jm-4NAF-VBiO-pQnY-etMWDclGv5un"),sQuery(id+"F4.wireOp",EDGE,"E118"),sQuery(id+"F4.wireOp",EDGE,"7M3HGg5D-aMQl-LYs1-MsCg-zVmLHFwYCo0C"),sQuery(id+"F4.wireOp",EDGE,"e6U4q213-1LtL-vwCs-wLTg-mGHH5etSdpE2"),sQuery(id+"F4.wireOp",EDGE,"E119"),sQuery(id+"F4.wireOp",EDGE,"E120"),sQuery(id+"F4.wireOp",EDGE,"E121"),sQuery(id+"F4.wireOp",EDGE,"E122"),sQuery(id+"F4.wireOp",EDGE,"R6Wk8btU-zCGi-4TmP-5Jjd-FV93XaIFImrj"),sQuery(id+"F4.wireOp",EDGE,"E123"),sQuery(id+"F4.wireOp",EDGE,"E124"),sQuery(id+"F4.wireOp",EDGE,"gRVzFYeP-EyGY-z86r-QQTZ-wZyysSSB34M7"),sQuery(id+"F4.wireOp",EDGE,"ylX56w3w-VO5M-fSch-uKYX-FYdjN5tmCMk0"),sQuery(id+"F4.wireOp",EDGE,"agFm78Yh-b6q2-hou8-vdYd-aVKsI7ZKnxmv"),sQuery(id+"F4.wireOp",EDGE,"Ipsl4LbN-QmTd-Wo4k-Iefa-eoOeaxQxMcxx"),sQuery(id+"F4.wireOp",EDGE,"aOvKBL3Z-v0oe-Nazm-0AOk-5JJxyVFELpqL"),sQuery(id+"F4.wireOp",EDGE,"PIPjAFRf-HRrE-UI3a-6rHr-U4BEnBnb3Jr0"),sQuery(id+"F4.wireOp",EDGE,"clCWdQkL-82pP-eXah-HGsn-A5WvFmz6JLAg"),sQuery(id+"F4.wireOp",EDGE,"E125"),sQuery(id+"F4.wireOp",EDGE,"E126"),sQuery(id+"F4.wireOp",EDGE,"E127"),sQuery(id+"F4.wireOp",EDGE,"E128"),sQuery(id+"F4.wireOp",EDGE,"2CZ2vCPZ-g25f-Aix0-Xy3j-dVw2FXJ3BshQ.bottom"),sQuery(id+"F4.wireOp",EDGE,"2CZ2vCPZ-g25f-Aix0-Xy3j-dVw2FXJ3BshQ.left"),sQuery(id+"F4.wireOp",EDGE,"2CZ2vCPZ-g25f-Aix0-Xy3j-dVw2FXJ3BshQ.right"),sQuery(id+"F4.wireOp",EDGE,"3PAsEz4y-MCME-JD8k-KRcV-DaMAZ5aYk3wh"),sQuery(id+"F4.wireOp",EDGE,"PkSCfb9l-bHuo-pSPV-febg-RSfLSyBgUNz0")])],"isStart":false});
            var sketch = newSketch(context, id + "F8", { "sketchPlane" : qUnion([Q0])});
            skLineSegment(sketch, "E222.bottom", {"start": v(-4.94, -140.75) * mm, "end": v(-5.94, -140.75) * mm});
            skLineSegment(sketch, "E222.top", {"start": v(-4.94, -208.97) * mm, "end": v(-5.94, -208.97) * mm});
            skLineSegment(sketch, "E222.left", {"start": v(-4.94, -140.75) * mm, "end": v(-4.94, -208.97) * mm});
            skLineSegment(sketch, "E222.right", {"start": v(-5.94, -140.75) * mm, "end": v(-5.94, -208.97) * mm});
            skLineSegment(sketch, "E223.bottom", {"start": v(-5.94, -208.97) * mm, "end": v(33.28, -208.97) * mm});
            skLineSegment(sketch, "E223.top", {"start": v(-5.94, -211.97) * mm, "end": v(33.28, -211.97) * mm});
            skLineSegment(sketch, "E223.left", {"start": v(-5.94, -208.97) * mm, "end": v(-5.94, -211.97) * mm});
            skLineSegment(sketch, "E223.right", {"start": v(33.28, -208.97) * mm, "end": v(33.28, -211.97) * mm});
            skLineSegment(sketch, "E224.bottom", {"start": v(33.28, -263.97) * mm, "end": v(30.28, -263.97) * mm});
            skLineSegment(sketch, "E224.top", {"start": v(33.28, -211.97) * mm, "end": v(30.28, -211.97) * mm});
            skLineSegment(sketch, "E224.left", {"start": v(33.28, -263.97) * mm, "end": v(33.28, -211.97) * mm});
            skLineSegment(sketch, "E224.right", {"start": v(30.28, -263.97) * mm, "end": v(30.28, -211.97) * mm});
            skLineSegment(sketch, "E225.bottom", {"start": v(182.06, -140.75) * mm, "end": v(183.06, -140.75) * mm});
            skLineSegment(sketch, "E225.top", {"start": v(182.06, -263.97) * mm, "end": v(183.06, -263.97) * mm});
            skLineSegment(sketch, "E225.left", {"start": v(182.06, -140.75) * mm, "end": v(182.06, -263.97) * mm});
            skLineSegment(sketch, "E225.right", {"start": v(183.06, -140.75) * mm, "end": v(183.06, -263.97) * mm});
            skLineSegment(sketch, "E226.bottom", {"start": v(183.06, -263.97) * mm, "end": v(169.06, -263.97) * mm});
            skLineSegment(sketch, "E226.top", {"start": v(183.06, -266.97) * mm, "end": v(169.06, -266.97) * mm});
            skLineSegment(sketch, "E226.left", {"start": v(183.06, -263.97) * mm, "end": v(183.06, -266.97) * mm});
            skLineSegment(sketch, "E226.right", {"start": v(169.06, -263.97) * mm, "end": v(169.06, -266.97) * mm});
            skLineSegment(sketch, "E227.bottom", {"start": v(153.56, -263.97) * mm, "end": v(118.56, -263.97) * mm});
            skLineSegment(sketch, "E227.top", {"start": v(153.56, -266.97) * mm, "end": v(118.56, -266.97) * mm});
            skLineSegment(sketch, "E227.left", {"start": v(153.56, -263.97) * mm, "end": v(153.56, -266.97) * mm});
            skLineSegment(sketch, "E227.right", {"start": v(118.56, -263.97) * mm, "end": v(118.56, -266.97) * mm});
            skLineSegment(sketch, "E228.bottom", {"start": v(30.28, -263.97) * mm, "end": v(102.28, -263.97) * mm});
            skLineSegment(sketch, "E228.top", {"start": v(30.28, -266.97) * mm, "end": v(102.28, -266.97) * mm});
            skLineSegment(sketch, "E228.left", {"start": v(30.28, -263.97) * mm, "end": v(30.28, -266.97) * mm});
            skLineSegment(sketch, "E228.right", {"start": v(102.28, -263.97) * mm, "end": v(102.28, -266.97) * mm});
            skLineSegment(sketch, "E229.bottom", {"start": v(118.56, -133.75) * mm, "end": v(119.56, -133.75) * mm});
            skLineSegment(sketch, "E229.top", {"start": v(118.56, -140.75) * mm, "end": v(119.56, -140.75) * mm});
            skLineSegment(sketch, "E229.left", {"start": v(118.56, -133.75) * mm, "end": v(118.56, -140.75) * mm});
            skLineSegment(sketch, "E229.right", {"start": v(119.56, -133.75) * mm, "end": v(119.56, -140.75) * mm});
            skLineSegment(sketch, "E230.bottom", {"start": v(58.56, -133.75) * mm, "end": v(57.56, -133.75) * mm});
            skLineSegment(sketch, "E230.top", {"start": v(58.56, -140.75) * mm, "end": v(57.56, -140.75) * mm});
            skLineSegment(sketch, "E230.left", {"start": v(58.56, -133.75) * mm, "end": v(58.56, -140.75) * mm});
            skLineSegment(sketch, "E230.right", {"start": v(57.56, -133.75) * mm, "end": v(57.56, -140.75) * mm});
            skSolve(sketch);
        }
        {
            var Q0;
            Q0=qSketchRegion(id+"F8",true);
            extrude(context, id + "F9", {"entities" : qUnion([Q0]), "operationType" : NewBodyOperationType.ADD, "oppositeDirection" : true, "depth" : 6 * mm});
        }
        {
            var Q0;
            Q0=makeQuery(id+"F9.opExtrude","SWEPT_EDGE",EDGE,{"disambiguationData":[OSD([sQuery(id+"F8.wireOp",EDGE,"E223.top"),sQuery(id+"F8.wireOp",EDGE,"E223.left")])]});
            var Q1;
            Q1=makeQuery(id+"F9.opExtrude","SWEPT_EDGE",EDGE,{"disambiguationData":[OSD([sQuery(id+"F8.wireOp",EDGE,"E223.top"),sQuery(id+"F8.wireOp",EDGE,"E224.top"),sQuery(id+"F8.wireOp",EDGE,"E224.right")])]});
            var Q2;
            Q2=makeQuery(id+"F9.opExtrude","SWEPT_EDGE",EDGE,{"disambiguationData":[OSD([sQuery(id+"F8.wireOp",EDGE,"E228.top"),sQuery(id+"F8.wireOp",EDGE,"E228.left")])]});
            var Q3;
            Q3=makeQuery(id+"F9.opExtrude","SWEPT_EDGE",EDGE,{"disambiguationData":[OSD([sQuery(id+"F8.wireOp",EDGE,"E226.top"),sQuery(id+"F8.wireOp",EDGE,"E226.left")])]});
            fillet(context, id + "F10", {"entities" : qUnion([Q0, Q1, Q2, Q3]), "radius" : 2 * mm, "tangentPropagation" : true, "allowEdgeOverflow" : false});
        }
        {
            var Q0;
            Q0=qSketchRegion(id+"F7",true);
            extrude(context, id + "F11", {"entities" : qUnion([Q0]), "operationType" : NewBodyOperationType.ADD, "oppositeDirection" : true, "depth" : 4 * mm});
        }
        {
            var Q0;
            {var subQ0=sQuery(id+"F4.wireOp",EDGE,"E132");var subQ1=sQuery(id+"F4.wireOp",EDGE,"E131");var subQ2=sQuery(id+"F4.wireOp",EDGE,"E130.top");Q0=makeQuery(id+"F11.boolean.opBoolean","SPLIT",FACE,{"disambiguationData":[TD([makeQuery(id+"F6.opExtrude","SWEPT_FACE",FACE,{"disambiguationData":[OSD([subQ2])]})])],"derivedFrom":makeQuery(id+"F6.opExtrude","CAP_FACE",FACE,{"disambiguationData":[OSD([sQuery(id+"F4.wireOp",EDGE,"E46.bottom"),sQuery(id+"F4.wireOp",EDGE,"E46.top"),sQuery(id+"F4.wireOp",EDGE,"E46.left"),sQuery(id+"F4.wireOp",EDGE,"E46.right"),sQuery(id+"F4.wireOp",EDGE,"E47"),sQuery(id+"F4.wireOp",EDGE,"E48"),sQuery(id+"F4.wireOp",EDGE,"E59"),sQuery(id+"F4.wireOp",EDGE,"E60"),sQuery(id+"F4.wireOp",EDGE,"E61"),sQuery(id+"F4.wireOp",EDGE,"E62"),sQuery(id+"F4.wireOp",EDGE,"E63"),sQuery(id+"F4.wireOp",EDGE,"E64"),sQuery(id+"F4.wireOp",EDGE,"E65"),sQuery(id+"F4.wireOp",EDGE,"E66"),sQuery(id+"F4.wireOp",EDGE,"E67"),sQuery(id+"F4.wireOp",EDGE,"E72"),sQuery(id+"F4.wireOp",EDGE,"E73"),sQuery(id+"F4.wireOp",EDGE,"E74"),sQuery(id+"F4.wireOp",EDGE,"E75"),sQuery(id+"F4.wireOp",EDGE,"E76"),sQuery(id+"F4.wireOp",EDGE,"CMYmPeaI-4HkP-dSsT-ciCo-EBNArNxvabU4"),sQuery(id+"F4.wireOp",EDGE,"UfYHLVnG-ZsXc-hSsb-096B-xReGw4xjWMuN"),sQuery(id+"F4.wireOp",EDGE,"LR1Smqzz-4zCy-jBud-aIPe-T4FdCvFcucQ2"),sQuery(id+"F4.wireOp",EDGE,"ZbBtRst9-qfY5-xJJi-duYC-lclwT5zfDQth"),sQuery(id+"F4.wireOp",EDGE,"8mlmSCBx-nmsO-8ibw-fLZu-H13SXNY5Fta6"),sQuery(id+"F4.wireOp",EDGE,"E85"),sQuery(id+"F4.wireOp",EDGE,"E86"),sQuery(id+"F4.wireOp",EDGE,"E87"),sQuery(id+"F4.wireOp",EDGE,"E88"),sQuery(id+"F4.wireOp",EDGE,"E89"),sQuery(id+"F4.wireOp",EDGE,"E90"),sQuery(id+"F4.wireOp",EDGE,"E91"),sQuery(id+"F4.wireOp",EDGE,"E92"),sQuery(id+"F4.wireOp",EDGE,"E93"),sQuery(id+"F4.wireOp",EDGE,"E94"),sQuery(id+"F4.wireOp",EDGE,"VxGM9Us5-GGZY-iukY-QufE-Hgw7Eb7M8YLq"),sQuery(id+"F4.wireOp",EDGE,"SQwhu13T-8Qlf-M2A9-FjbU-sqE2fhrdCHsq"),sQuery(id+"F4.wireOp",EDGE,"boMX5wRL-iCUG-njbD-9Rz0-iznqWW2C3mA9"),sQuery(id+"F4.wireOp",EDGE,"8wUrnrco-ptQb-soB3-ZJPL-oLVazxcvUS0h"),sQuery(id+"F4.wireOp",EDGE,"HpmNjthl-ehj3-1CQD-7Ubw-BaRG0imoQFcp"),sQuery(id+"F4.wireOp",EDGE,"E95"),sQuery(id+"F4.wireOp",EDGE,"E96"),sQuery(id+"F4.wireOp",EDGE,"E97"),sQuery(id+"F4.wireOp",EDGE,"E98"),sQuery(id+"F4.wireOp",EDGE,"E99"),sQuery(id+"F4.wireOp",EDGE,"E100"),sQuery(id+"F4.wireOp",EDGE,"E101"),sQuery(id+"F4.wireOp",EDGE,"E102"),sQuery(id+"F4.wireOp",EDGE,"E103"),sQuery(id+"F4.wireOp",EDGE,"E104"),sQuery(id+"F4.wireOp",EDGE,"E105"),sQuery(id+"F4.wireOp",EDGE,"E106"),sQuery(id+"F4.wireOp",EDGE,"E107"),sQuery(id+"F4.wireOp",EDGE,"E108"),sQuery(id+"F4.wireOp",EDGE,"E109"),sQuery(id+"F4.wireOp",EDGE,"E110"),sQuery(id+"F4.wireOp",EDGE,"E111"),sQuery(id+"F4.wireOp",EDGE,"E112"),sQuery(id+"F4.wireOp",EDGE,"E113"),sQuery(id+"F4.wireOp",EDGE,"E114"),sQuery(id+"F4.wireOp",EDGE,"E115"),sQuery(id+"F4.wireOp",EDGE,"E116"),sQuery(id+"F4.wireOp",EDGE,"E117"),sQuery(id+"F4.wireOp",EDGE,"E118"),sQuery(id+"F4.wireOp",EDGE,"E119"),sQuery(id+"F4.wireOp",EDGE,"E120"),sQuery(id+"F4.wireOp",EDGE,"E121"),sQuery(id+"F4.wireOp",EDGE,"E122"),sQuery(id+"F4.wireOp",EDGE,"E123"),sQuery(id+"F4.wireOp",EDGE,"E124"),sQuery(id+"F4.wireOp",EDGE,"E125"),sQuery(id+"F4.wireOp",EDGE,"E126"),sQuery(id+"F4.wireOp",EDGE,"E127"),sQuery(id+"F4.wireOp",EDGE,"E128"),sQuery(id+"F4.wireOp",EDGE,"PkSCfb9l-bHuo-pSPV-febg-RSfLSyBgUNz0"),sQuery(id+"F4.wireOp",EDGE,"E129"),subQ2,sQuery(id+"F4.wireOp",EDGE,"E130.left"),sQuery(id+"F4.wireOp",EDGE,"E130.right"),subQ1,subQ0,sQuery(id+"F4.wireOp",EDGE,"E133"),sQuery(id+"F4.wireOp",EDGE,"E135"),sQuery(id+"F4.wireOp",EDGE,"E136"),sQuery(id+"F4.wireOp",EDGE,"E137"),sQuery(id+"F4.wireOp",EDGE,"E138"),sQuery(id+"F4.wireOp",EDGE,"E139"),sQuery(id+"F4.wireOp",EDGE,"E140"),sQuery(id+"F4.wireOp",EDGE,"E141"),sQuery(id+"F4.wireOp",EDGE,"E143"),sQuery(id+"F4.wireOp",EDGE,"E144"),sQuery(id+"F4.wireOp",EDGE,"E145"),sQuery(id+"F4.wireOp",EDGE,"E146"),sQuery(id+"F4.wireOp",EDGE,"E147"),sQuery(id+"F4.wireOp",EDGE,"E148"),sQuery(id+"F4.wireOp",EDGE,"E149"),sQuery(id+"F4.wireOp",EDGE,"E150"),sQuery(id+"F4.wireOp",EDGE,"E151"),sQuery(id+"F4.wireOp",EDGE,"E152"),sQuery(id+"F4.wireOp",EDGE,"E153"),sQuery(id+"F4.wireOp",EDGE,"E154"),sQuery(id+"F4.wireOp",EDGE,"E155")])],"isStart":true})});}
            extrude(context, id + "F12", {"entities" : qUnion([Q0]), "operationType" : NewBodyOperationType.ADD, "depth" : 4 * mm});
        }
    });
